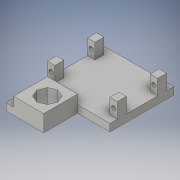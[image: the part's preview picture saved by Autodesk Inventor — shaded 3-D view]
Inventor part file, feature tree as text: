
AUTODESK INVENTOR PART (.ipt)
format: ipt  version: 2016 (Build 200138000, 138)  size: 198,144 bytes
history: native  units: in
note: dims shown in document units (in); Inventor stores cm internally (conversion verified against a paired STEP export)
features: extrude x5, sketch x5, shell x1
ambient origin geometry x8: Origin, YZ Plane, XZ Plane, XY Plane, X Axis, Y Axis, Z Axis, Center Point
bodies: Solid1 (feature_tree)
feature tree (11):
  extrude  "Extrusion1"  Depth=1.264in
  extrude  "Extrusion2"  Depth=2.3545in
  extrude  "Extrusion3"  Depth=1.9in
  extrude  "Extrusion4"  Depth=0.3in
  extrude  "Extrusion5"  Depth=0.25in
  shell  "Shell1"  Thickness=0.25in
  sketch  "Sketch1"  dims[d0=1.1408in d1=1.264in]
  sketch  "Sketch2"  dims[d6=0.56in d7=0.0in d8=2.3545in]
  sketch  "Sketch3"  dims[d9=0.25in d10=1.9in]
  sketch  "Sketch4"  dims[d11=0.25in d12=0.3in]
  sketch  "Sketch5"  dims[d13=0.25in d14=0.25in d15=0.25in d16=0.3in d17=0.25in d18=0.0in d19=0.25in d20=0.25in d21=0.3in d22=0.25in d23=0.3in d26=0.25in d27=0.512in d28=0.0in d29=2.5505in d30=0.0in d31=0.148in d32=0.148in d33=7.238in d34=0.0in d35=0.2in]
